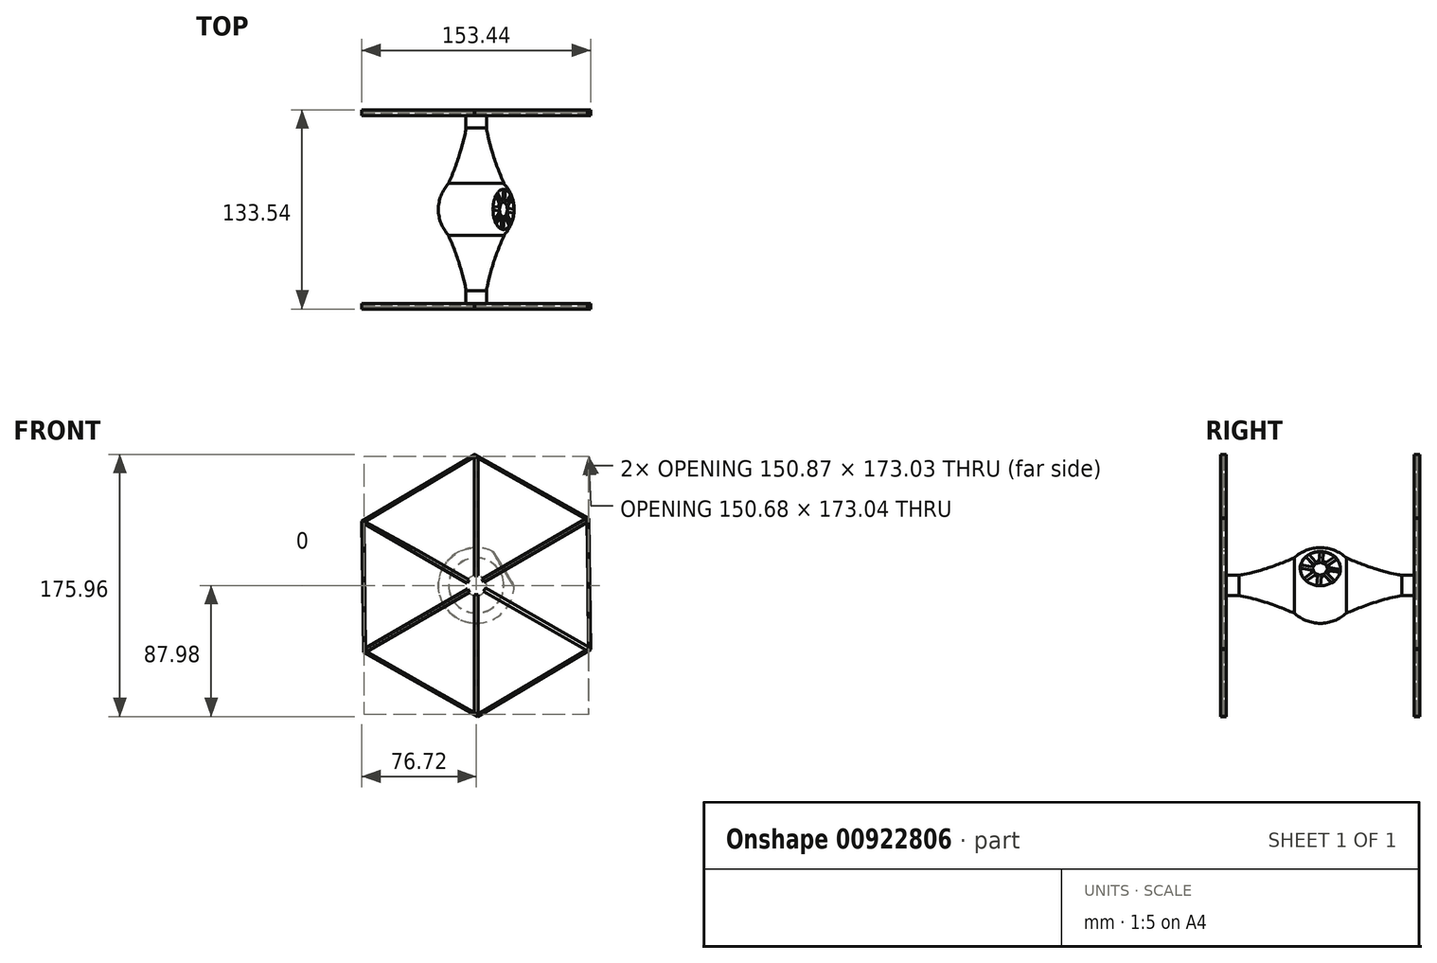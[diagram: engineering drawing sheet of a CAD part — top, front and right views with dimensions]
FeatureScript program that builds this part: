
annotation { "Feature Type Name" : "Feature", "Feature Type Description" : "" }
export const myFeature = defineFeature(function(context is Context, id is Id, definition is map)
    precondition{}
    {
        {
            var Q0;
            Q0=qCreatedBy(makeId("Front.planeOp"),FACE);
            var sketch = newSketch(context, id + "F0", { "sketchPlane" : qUnion([Q0])});
            skArc(sketch, "E0", {"start": v(0, 25.4) * mm, "mid": v(25.4, 0) * mm, "end": v(0, -25.4) * mm});
            skLineSegment(sketch, "E1", {"start": v(0, 25.4) * mm, "end": v(0, -25.4) * mm});
            skSolve(sketch);
        }
        {
            var Q0;
            Q0=qSketchRegion(id+"F0",true);
            var Q1;
            Q1=sQuery(id+"F0.wireOp",EDGE,"E1");
            revolve(context, id + "F1", {"surfaceOperationType" : NewSurfaceOperationType.NEW, "entities" : qUnion([Q0]), "axis" : qUnion([Q1]), "revolveType" : RevolveType.ONE_DIRECTION, "angle" : 180 * degree});
        }
        {
            var Q0;
            Q0=qCreatedBy(makeId("Right.planeOp"),FACE);
            var sketch = newSketch(context, id + "F2", { "sketchPlane" : qUnion([Q0])});
            skLineSegment(sketch, "E2", {"start": v(-62.96, 0) * mm, "end": v(0, 0) * mm});
            skLineSegment(sketch, "E3", {"start": v(-62.96, 0) * mm, "end": v(-62.96, 6.88) * mm});
            skFitSpline(sketch, "E4", {"points": [v(-62.96, 6.88) * mm, v(-54.61, 6.88) * mm, v(-33.5, 12.3) * mm, v(-17.49, 18.56) * mm], "startDerivative": vector(40.65, 0) * mm, "endDerivative": vector(41.74, 17.6) * mm});
            skLineSegment(sketch, "E5", {"start": v(-17.49, 18.56) * mm, "end": v(-17.49, 0) * mm});
            skLineSegment(sketch, "E6", {"start": v(-62.96, 6.88) * mm, "end": v(-50.15, 6.88) * mm});
            skSolve(sketch);
        }
        {
            var Q0;
            Q0=qSketchRegion(id+"F2",true);
            var Q1;
            Q1=sQuery(id+"F2.wireOp",EDGE,"E2");
            revolve(context, id + "F3", {"operationType" : NewBodyOperationType.ADD, "surfaceOperationType" : NewSurfaceOperationType.NEW, "entities" : qUnion([Q0]), "axis" : qUnion([Q1]), "revolveType" : RevolveType.FULL});
        }
        {
            var Q0;
            Q0=qCreatedBy(makeId("Front.planeOp"),FACE);
            var sketch = newSketch(context, id + "F4", { "sketchPlane" : qUnion([Q0])});
            skLineSegment(sketch, "E7", {"start": v(18.07, 11.14) * mm, "end": v(0, 0) * mm});
            skSolve(sketch);
        }
        {
            var Q0;
            Q0=makeQuery(id+"F3.opRevolve","SWEPT_FACE",FACE,{"disambiguationData":[OSD([sQuery(id+"F2.wireOp",EDGE,"E3")])]});
            cPlane(context, id + "F5", {"entities" : qUnion([Q0]), "cplaneType" : CPlaneType.OFFSET, "offset" : 0 * mm, "width" : 152.4 * mm, "height" : 152.4 * mm});
        }
        {
            var Q0;
            Q0=qCreatedBy(id+"F5.planeOp",FACE);
            var sketch = newSketch(context, id + "F6", { "sketchPlane" : qUnion([Q0])});
            skCircle(sketch, "E8.cCircle", {"center": v(0, 0) * mm, "radius": 76.2 * mm, "construction": true});
            skLineSegment(sketch, "E8.0", {"start": v(76.62, -43.26) * mm, "end": v(0.84, -87.98) * mm});
            skLineSegment(sketch, "E8.1", {"start": v(0.84, -87.98) * mm, "end": v(-75.78, -44.72) * mm});
            skLineSegment(sketch, "E8.2", {"start": v(-75.78, -44.72) * mm, "end": v(-76.62, 43.26) * mm});
            skLineSegment(sketch, "E8.3", {"start": v(-76.62, 43.26) * mm, "end": v(-0.84, 87.98) * mm});
            skLineSegment(sketch, "E8.4", {"start": v(-0.84, 87.98) * mm, "end": v(75.78, 44.72) * mm});
            skLineSegment(sketch, "E8.5", {"start": v(75.78, 44.72) * mm, "end": v(76.62, -43.26) * mm});
            skPoint(sketch, "E8.0.midPoint", {"position": v(38.73, -65.62) * mm});
            skSolve(sketch);
        }
        {
            var Q0;
            Q0=qSketchRegion(id+"F6",true);
            extrude(context, id + "F7", {"entities" : qUnion([Q0]), "depth" : 2.54 * mm, "offsetDistance" : 25.4 * mm});
        }
        {
            var Q0;
            Q0=makeQuery(id+"F7.opExtrude","CAP_FACE",FACE,{"disambiguationData":[OSD([sQuery(id+"F6.wireOp",EDGE,"E8.0"),sQuery(id+"F6.wireOp",EDGE,"E8.1"),sQuery(id+"F6.wireOp",EDGE,"E8.2"),sQuery(id+"F6.wireOp",EDGE,"E8.3"),sQuery(id+"F6.wireOp",EDGE,"E8.4"),sQuery(id+"F6.wireOp",EDGE,"E8.5")])],"isStart":false});
            shell(context, id + "F8", {"entities" : qUnion([Q0]), "thickness" : 1.27 * mm});
        }
        {
            var Q0;
            Q0=qCreatedBy(id+"F5.planeOp",FACE);
            var sketch = newSketch(context, id + "F9", { "sketchPlane" : qUnion([Q0])});
            skLineSegment(sketch, "E9", {"start": v(0, 92.99) * mm, "end": v(0, 6.47) * mm, "construction": true});
            skLineSegment(sketch, "E10", {"start": v(-80.5, 45.9) * mm, "end": v(-5.53, 2.72) * mm, "construction": true});
            skLineSegment(sketch, "E11", {"start": v(5.53, -2.69) * mm, "end": v(80.5, -45.88) * mm, "construction": true});
            skLineSegment(sketch, "E12", {"start": v(0, -6.03) * mm, "end": v(0, -92.55) * mm});
            skLineSegment(sketch, "E13", {"start": v(-80, -46.75) * mm, "end": v(-5.12, -3.4) * mm, "construction": true});
            skLineSegment(sketch, "E14", {"start": v(4.34, 3.22) * mm, "end": v(79.21, 46.57) * mm, "construction": true});
            skLineSegment(sketch, "E15", {"start": v(-1.27, -6.03) * mm, "end": v(1.27, -6.03) * mm});
            skLineSegment(sketch, "E16", {"start": v(4.9, -3.79) * mm, "end": v(6.17, -1.59) * mm});
            skLineSegment(sketch, "E17", {"start": v(3.7, 4.32) * mm, "end": v(4.97, 2.12) * mm});
            skLineSegment(sketch, "E18", {"start": v(3.7, 4.32) * mm, "end": v(78.58, 47.67) * mm});
            skLineSegment(sketch, "E19", {"start": v(4.97, 2.12) * mm, "end": v(79.85, 45.47) * mm});
            skLineSegment(sketch, "E20", {"start": v(-1.27, 6.47) * mm, "end": v(1.27, 6.47) * mm});
            skLineSegment(sketch, "E21", {"start": v(-6.17, 1.62) * mm, "end": v(-4.9, 3.82) * mm});
            skLineSegment(sketch, "E22", {"start": v(-4.4, -4.44) * mm, "end": v(-5.84, -2.36) * mm});
            skLineSegment(sketch, "E23", {"start": v(-4.9, 3.82) * mm, "end": v(-38.95, 23.43) * mm});
            skLineSegment(sketch, "E24", {"start": v(-6.17, 1.62) * mm, "end": v(-81.14, 44.8) * mm});
            skLineSegment(sketch, "E25", {"start": v(-4.4, -4.44) * mm, "end": v(-79.27, -47.8) * mm});
            skLineSegment(sketch, "E26", {"start": v(-5.84, -2.36) * mm, "end": v(-80, -45.29) * mm});
            skLineSegment(sketch, "E27", {"start": v(4.9, -3.79) * mm, "end": v(79.87, -46.98) * mm});
            skLineSegment(sketch, "E28", {"start": v(6.17, -1.59) * mm, "end": v(81.14, -44.78) * mm});
            skLineSegment(sketch, "E29", {"start": v(-1.27, 6.47) * mm, "end": v(-1.27, 92.99) * mm});
            skLineSegment(sketch, "E30", {"start": v(1.27, 6.47) * mm, "end": v(1.27, 92.99) * mm});
            skLineSegment(sketch, "E31", {"start": v(1.27, -6.03) * mm, "end": v(1.27, -92.55) * mm});
            skLineSegment(sketch, "E32", {"start": v(-1.27, -6.03) * mm, "end": v(-1.27, -92.55) * mm});
            skLineSegment(sketch, "E33", {"start": v(1.27, -92.55) * mm, "end": v(0, -92.55) * mm});
            skLineSegment(sketch, "E34", {"start": v(0, -92.55) * mm, "end": v(-1.27, -92.55) * mm});
            skLineSegment(sketch, "E35", {"start": v(81.14, -44.78) * mm, "end": v(80.5, -45.88) * mm});
            skLineSegment(sketch, "E36", {"start": v(79.87, -46.98) * mm, "end": v(80.5, -45.88) * mm});
            skLineSegment(sketch, "E37", {"start": v(79.21, 46.57) * mm, "end": v(79.85, 45.47) * mm});
            skLineSegment(sketch, "E38", {"start": v(79.21, 46.57) * mm, "end": v(78.58, 47.67) * mm});
            skLineSegment(sketch, "E39", {"start": v(1.27, 92.99) * mm, "end": v(0, 92.99) * mm});
            skLineSegment(sketch, "E40", {"start": v(-1.27, 92.99) * mm, "end": v(0, 92.99) * mm});
            skLineSegment(sketch, "E41", {"start": v(0, 92.99) * mm, "end": v(-1.27, 92.99) * mm});
            skLineSegment(sketch, "E42", {"start": v(-81.14, 44.8) * mm, "end": v(-80.5, 45.9) * mm});
            skLineSegment(sketch, "E43", {"start": v(-38.95, 23.43) * mm, "end": v(-80.5, 45.9) * mm});
            skLineSegment(sketch, "E44", {"start": v(-80, -45.29) * mm, "end": v(-80, -46.75) * mm});
            skLineSegment(sketch, "E45", {"start": v(-79.27, -47.8) * mm, "end": v(-80, -46.75) * mm});
            skSolve(sketch);
        }
        {
            var Q0;
            Q0=qSketchRegion(id+"F9",true);
            extrude(context, id + "F10", {"entities" : qUnion([Q0]), "depth" : 2.54 * mm, "offsetDistance" : 25.4 * mm});
        }
        {
            var Q0;
            Q0=qCreatedBy(id+"F5.planeOp",FACE);
            var sketch = newSketch(context, id + "F11", { "sketchPlane" : qUnion([Q0])});
            skCircle(sketch, "E46.cCircle", {"center": v(0, 0) * mm, "radius": 76.2 * mm, "construction": true});
            skLineSegment(sketch, "E46.0", {"start": v(1.03, -87.98) * mm, "end": v(-75.68, -44.89) * mm});
            skLineSegment(sketch, "E46.1", {"start": v(-75.68, -44.89) * mm, "end": v(-76.71, 43.1) * mm});
            skLineSegment(sketch, "E46.2", {"start": v(-76.71, 43.1) * mm, "end": v(-1.03, 87.98) * mm});
            skLineSegment(sketch, "E46.3", {"start": v(-1.03, 87.98) * mm, "end": v(75.68, 44.89) * mm});
            skLineSegment(sketch, "E46.4", {"start": v(75.68, 44.89) * mm, "end": v(76.71, -43.1) * mm});
            skLineSegment(sketch, "E46.5", {"start": v(76.71, -43.1) * mm, "end": v(1.03, -87.98) * mm});
            skPoint(sketch, "E46.0.midPoint", {"position": v(-37.32, -66.43) * mm});
            skCircle(sketch, "E47.cCircle", {"center": v(0, 0) * mm, "radius": 74.93 * mm, "construction": true});
            skLineSegment(sketch, "E47.0", {"start": v(75.43, -42.38) * mm, "end": v(1.02, -86.52) * mm});
            skLineSegment(sketch, "E47.1", {"start": v(1.02, -86.52) * mm, "end": v(-74.42, -44.14) * mm});
            skLineSegment(sketch, "E47.2", {"start": v(-74.42, -44.14) * mm, "end": v(-75.43, 42.38) * mm});
            skLineSegment(sketch, "E47.3", {"start": v(-75.43, 42.38) * mm, "end": v(-1.02, 86.52) * mm});
            skLineSegment(sketch, "E47.4", {"start": v(-1.02, 86.52) * mm, "end": v(74.42, 44.14) * mm});
            skLineSegment(sketch, "E47.5", {"start": v(74.42, 44.14) * mm, "end": v(75.43, -42.38) * mm});
            skPoint(sketch, "E47.0.midPoint", {"position": v(38.23, -64.45) * mm});
            skLineSegment(sketch, "E48", {"start": v(0, 0) * mm, "end": v(-1.02, 86.52) * mm, "construction": true});
            skSolve(sketch);
        }
        {
            var Q0;
            Q0=qSketchRegion(id+"F11",true);
            extrude(context, id + "F12", {"entities" : qUnion([Q0]), "depth" : 3.8 * mm, "offsetDistance" : 25.4 * mm});
        }
        {
            var Q0;
            Q0=qCreatedBy(id+"F5.planeOp",FACE);
            var sketch = newSketch(context, id + "F13", { "sketchPlane" : qUnion([Q0])});
            skCircle(sketch, "E49.cCircle", {"center": v(0, 0) * mm, "radius": 76.2 * mm, "construction": true});
            skLineSegment(sketch, "E49.0", {"start": v(1.05, -87.98) * mm, "end": v(-75.67, -44.9) * mm});
            skLineSegment(sketch, "E49.1", {"start": v(-75.67, -44.9) * mm, "end": v(-76.72, 43.08) * mm});
            skLineSegment(sketch, "E49.2", {"start": v(-76.72, 43.08) * mm, "end": v(-1.05, 87.98) * mm});
            skLineSegment(sketch, "E49.3", {"start": v(-1.05, 87.98) * mm, "end": v(75.67, 44.9) * mm});
            skLineSegment(sketch, "E49.4", {"start": v(75.67, 44.9) * mm, "end": v(76.72, -43.08) * mm});
            skLineSegment(sketch, "E49.5", {"start": v(76.72, -43.08) * mm, "end": v(1.05, -87.98) * mm});
            skPoint(sketch, "E49.0.midPoint", {"position": v(-37.31, -66.44) * mm});
            skCircle(sketch, "E50.cCircle", {"center": v(0, 0) * mm, "radius": 151.68 * mm, "construction": true});
            skLineSegment(sketch, "E50.0", {"start": v(-149.87, -90.64) * mm, "end": v(-153.43, 84.47) * mm});
            skLineSegment(sketch, "E50.1", {"start": v(-153.43, 84.47) * mm, "end": v(-3.56, 175.11) * mm});
            skLineSegment(sketch, "E50.2", {"start": v(-3.56, 175.11) * mm, "end": v(149.87, 90.64) * mm});
            skLineSegment(sketch, "E50.3", {"start": v(149.87, 90.64) * mm, "end": v(153.43, -84.47) * mm});
            skLineSegment(sketch, "E50.4", {"start": v(153.43, -84.47) * mm, "end": v(3.56, -175.11) * mm});
            skLineSegment(sketch, "E50.5", {"start": v(3.56, -175.11) * mm, "end": v(-149.87, -90.64) * mm});
            skPoint(sketch, "E50.0.midPoint", {"position": v(-151.65, -3.09) * mm});
            skSolve(sketch);
        }
        {
            var Q0;
            Q0=qSketchRegion(id+"F13",true);
            extrude(context, id + "F14", {"entities" : qUnion([Q0]), "operationType" : NewBodyOperationType.REMOVE, "depth" : 101.6 * mm, "offsetDistance" : 25.4 * mm});
        }
        {
            var Q0;
            Q0=makeQuery(id+"F1.opRevolve","SWEPT_BODY",BODY,{"disambiguationData":[OSD([sQuery(id+"F0.wireOp",EDGE,"E0"),sQuery(id+"F0.wireOp",EDGE,"E1")])]});
            var Q1;
            Q1=makeQuery(id+"F12.opExtrude","SWEPT_BODY",BODY,{"disambiguationData":[OSD([sQuery(id+"F11.wireOp",EDGE,"E46.0"),sQuery(id+"F11.wireOp",EDGE,"E46.1"),sQuery(id+"F11.wireOp",EDGE,"E46.2"),sQuery(id+"F11.wireOp",EDGE,"E46.3"),sQuery(id+"F11.wireOp",EDGE,"E46.4"),sQuery(id+"F11.wireOp",EDGE,"E46.5"),sQuery(id+"F11.wireOp",EDGE,"E47.0"),sQuery(id+"F11.wireOp",EDGE,"E47.1"),sQuery(id+"F11.wireOp",EDGE,"E47.2"),sQuery(id+"F11.wireOp",EDGE,"E47.3"),sQuery(id+"F11.wireOp",EDGE,"E47.4"),sQuery(id+"F11.wireOp",EDGE,"E47.5")])]});
            var Q2;
            Q2=makeQuery(id+"F10.opExtrude","SWEPT_BODY",BODY,{"disambiguationData":[OSD([sQuery(id+"F9.wireOp",EDGE,"E17"),sQuery(id+"F9.wireOp",EDGE,"E18"),sQuery(id+"F9.wireOp",EDGE,"E19"),sQuery(id+"F9.wireOp",EDGE,"E37"),sQuery(id+"F9.wireOp",EDGE,"E38")])]});
            var Q3;
            Q3=makeQuery(id+"F7.opExtrude","SWEPT_BODY",BODY,{"disambiguationData":[OSD([sQuery(id+"F6.wireOp",EDGE,"E8.0"),sQuery(id+"F6.wireOp",EDGE,"E8.1"),sQuery(id+"F6.wireOp",EDGE,"E8.2"),sQuery(id+"F6.wireOp",EDGE,"E8.3"),sQuery(id+"F6.wireOp",EDGE,"E8.4"),sQuery(id+"F6.wireOp",EDGE,"E8.5")])]});
            var Q4;
            Q4=makeQuery(id+"F10.opExtrude","SWEPT_BODY",BODY,{"disambiguationData":[OSD([sQuery(id+"F9.wireOp",EDGE,"E16"),sQuery(id+"F9.wireOp",EDGE,"E27"),sQuery(id+"F9.wireOp",EDGE,"E28"),sQuery(id+"F9.wireOp",EDGE,"E35"),sQuery(id+"F9.wireOp",EDGE,"E36")])]});
            var Q5;
            Q5=makeQuery(id+"F10.opExtrude","SWEPT_BODY",BODY,{"disambiguationData":[OSD([sQuery(id+"F9.wireOp",EDGE,"E15"),sQuery(id+"F9.wireOp",EDGE,"E31"),sQuery(id+"F9.wireOp",EDGE,"E32"),sQuery(id+"F9.wireOp",EDGE,"E33"),sQuery(id+"F9.wireOp",EDGE,"E34")])]});
            var Q6;
            Q6=makeQuery(id+"F10.opExtrude","SWEPT_BODY",BODY,{"disambiguationData":[OSD([sQuery(id+"F9.wireOp",EDGE,"E21"),sQuery(id+"F9.wireOp",EDGE,"E23"),sQuery(id+"F9.wireOp",EDGE,"E24"),sQuery(id+"F9.wireOp",EDGE,"E42"),sQuery(id+"F9.wireOp",EDGE,"E43")])]});
            var Q7;
            Q7=makeQuery(id+"F10.opExtrude","SWEPT_BODY",BODY,{"disambiguationData":[OSD([sQuery(id+"F9.wireOp",EDGE,"E20"),sQuery(id+"F9.wireOp",EDGE,"E29"),sQuery(id+"F9.wireOp",EDGE,"E30"),sQuery(id+"F9.wireOp",EDGE,"E39"),sQuery(id+"F9.wireOp",EDGE,"E41")])]});
            var Q8;
            Q8=makeQuery(id+"F10.opExtrude","SWEPT_BODY",BODY,{"disambiguationData":[OSD([sQuery(id+"F9.wireOp",EDGE,"E22"),sQuery(id+"F9.wireOp",EDGE,"E25"),sQuery(id+"F9.wireOp",EDGE,"E26"),sQuery(id+"F9.wireOp",EDGE,"E44"),sQuery(id+"F9.wireOp",EDGE,"E45")])]});
            var Q9;
            Q9=qCreatedBy(makeId("Front.planeOp"),FACE);
            mirror(context, id + "F15", {"entities" : qUnion([Q0, Q1, Q2, Q3, Q4, Q5, Q6, Q7, Q8]), "mirrorPlane" : qUnion([Q9])});
        }
        {
            var Q0;
            Q0=sQuery(id+"F4.wireOp",VERTEX,"E7.start");
            var Q1;
            Q1=sQuery(id+"F4.wireOp",EDGE,"E7");
            cPlane(context, id + "F16", {"entities" : qUnion([Q0, Q1]), "cplaneType" : CPlaneType.CURVE_POINT, "offset" : 25.4 * mm, "width" : 152.4 * mm, "height" : 152.4 * mm});
        }
        {
            var Q0;
            Q0=qCreatedBy(id+"F16.planeOp",FACE);
            var sketch = newSketch(context, id + "F17", { "sketchPlane" : qUnion([Q0])});
            skCircle(sketch, "E51", {"center": v(0, 0) * mm, "radius": 13.5 * mm});
            skSolve(sketch);
        }
        {
            var Q0;
            Q0=qSketchRegion(id+"F17",true);
            extrude(context, id + "F18", {"entities" : qUnion([Q0]), "operationType" : NewBodyOperationType.REMOVE, "oppositeDirection" : true, "depth" : 25.4 * mm, "offsetDistance" : 25.4 * mm});
        }
        {
            var Q0;
            Q0=qCreatedBy(id+"F16.planeOp",FACE);
            var sketch = newSketch(context, id + "F19", { "sketchPlane" : qUnion([Q0])});
            skCircle(sketch, "E52.cCircle", {"center": v(0, 0) * mm, "radius": 6.1 * mm, "construction": true});
            skLineSegment(sketch, "E52.0", {"start": v(0.45, -6.6) * mm, "end": v(-4.34, -4.98) * mm});
            skLineSegment(sketch, "E52.1", {"start": v(-4.34, -4.98) * mm, "end": v(-6.6, -0.45) * mm});
            skLineSegment(sketch, "E52.2", {"start": v(-6.6, -0.45) * mm, "end": v(-4.98, 4.34) * mm});
            skLineSegment(sketch, "E52.3", {"start": v(-4.98, 4.34) * mm, "end": v(-0.45, 6.6) * mm});
            skLineSegment(sketch, "E52.4", {"start": v(-0.45, 6.6) * mm, "end": v(4.34, 4.98) * mm});
            skLineSegment(sketch, "E52.5", {"start": v(4.34, 4.98) * mm, "end": v(6.6, 0.45) * mm});
            skLineSegment(sketch, "E52.6", {"start": v(6.6, 0.45) * mm, "end": v(4.98, -4.34) * mm});
            skLineSegment(sketch, "E52.7", {"start": v(4.98, -4.34) * mm, "end": v(0.45, -6.6) * mm});
            skPoint(sketch, "E52.0.midPoint", {"position": v(-1.95, -5.78) * mm});
            skLineSegment(sketch, "E53", {"start": v(-0.45, 6.6) * mm, "end": v(-0.87, 13.38) * mm, "construction": true});
            skLineSegment(sketch, "E54", {"start": v(4.34, 4.98) * mm, "end": v(8.62, 10.27) * mm, "construction": true});
            skLineSegment(sketch, "E55", {"start": v(-4.98, 4.34) * mm, "end": v(-10.46, 8.47) * mm, "construction": true});
            skLineSegment(sketch, "E56", {"start": v(-6.6, -0.45) * mm, "end": v(-13.35, -1.73) * mm, "construction": true});
            skLineSegment(sketch, "E57", {"start": v(-4.34, -4.98) * mm, "end": v(-8.67, -10.4) * mm, "construction": true});
            skLineSegment(sketch, "E58", {"start": v(0.45, -6.6) * mm, "end": v(1.08, -13.42) * mm, "construction": true});
            skLineSegment(sketch, "E59", {"start": v(4.98, -4.34) * mm, "end": v(10.28, -8.68) * mm, "construction": true});
            skLineSegment(sketch, "E60", {"start": v(6.6, 0.45) * mm, "end": v(13.35, 1.77) * mm, "construction": true});
            skLineSegment(sketch, "E61", {"start": v(7.59, 11.13) * mm, "end": v(9.66, 9.42) * mm});
            skLineSegment(sketch, "E62", {"start": v(7.59, 11.13) * mm, "end": v(2.92, 5.46) * mm});
            skLineSegment(sketch, "E63", {"start": v(9.66, 9.42) * mm, "end": v(5, 3.66) * mm});
            skLineSegment(sketch, "E64", {"start": v(-2.1, 13.3) * mm, "end": v(0.37, 13.45) * mm});
            skLineSegment(sketch, "E65", {"start": v(-2.1, 13.3) * mm, "end": v(-1.65, 6) * mm});
            skLineSegment(sketch, "E66", {"start": v(0.37, 13.45) * mm, "end": v(0.8, 6.17) * mm});
            skCircle(sketch, "E67.cCircle", {"center": v(0, 0) * mm, "radius": 4.83 * mm, "construction": true});
            skLineSegment(sketch, "E67.0", {"start": v(4, -3.37) * mm, "end": v(0.45, -5.21) * mm});
            skLineSegment(sketch, "E67.1", {"start": v(0.45, -5.21) * mm, "end": v(-3.37, -4) * mm});
            skLineSegment(sketch, "E67.2", {"start": v(-3.37, -4) * mm, "end": v(-5.21, -0.45) * mm});
            skLineSegment(sketch, "E67.3", {"start": v(-5.21, -0.45) * mm, "end": v(-4, 3.37) * mm});
            skLineSegment(sketch, "E67.4", {"start": v(-4, 3.37) * mm, "end": v(-0.45, 5.21) * mm});
            skLineSegment(sketch, "E67.5", {"start": v(-0.45, 5.21) * mm, "end": v(3.37, 4) * mm});
            skLineSegment(sketch, "E67.6", {"start": v(3.37, 4) * mm, "end": v(5.21, 0.45) * mm});
            skLineSegment(sketch, "E67.7", {"start": v(5.21, 0.45) * mm, "end": v(4, -3.37) * mm});
            skPoint(sketch, "E67.0.midPoint", {"position": v(2.23, -4.3) * mm});
            skLineSegment(sketch, "E68", {"start": v(-11.23, 7.47) * mm, "end": v(-9.7, 9.47) * mm});
            skLineSegment(sketch, "E69", {"start": v(-9.7, 9.47) * mm, "end": v(-3.79, 4.93) * mm});
            skLineSegment(sketch, "E70", {"start": v(-11.23, 7.47) * mm, "end": v(-5.43, 3) * mm});
            skLineSegment(sketch, "E71", {"start": v(-13.57, -0.58) * mm, "end": v(-13.13, -2.87) * mm});
            skLineSegment(sketch, "E72", {"start": v(-13.13, -2.87) * mm, "end": v(-6.05, -1.53) * mm});
            skLineSegment(sketch, "E73", {"start": v(-13.57, -0.58) * mm, "end": v(-6.16, 0.82) * mm});
            skLineSegment(sketch, "E74", {"start": v(-9.64, -9.57) * mm, "end": v(-7.71, -11.23) * mm});
            skLineSegment(sketch, "E75", {"start": v(-9.64, -9.57) * mm, "end": v(-4.83, -4) * mm});
            skLineSegment(sketch, "E76", {"start": v(-7.71, -11.23) * mm, "end": v(-3.06, -5.4) * mm});
            skLineSegment(sketch, "E77", {"start": v(2.34, -13.3) * mm, "end": v(-0.19, -13.53) * mm});
            skLineSegment(sketch, "E78", {"start": v(-0.19, -13.53) * mm, "end": v(-0.87, -6.15) * mm});
            skLineSegment(sketch, "E79", {"start": v(2.34, -13.3) * mm, "end": v(1.67, -5.99) * mm});
            skLineSegment(sketch, "E80", {"start": v(9.46, -9.68) * mm, "end": v(11.1, -7.67) * mm});
            skLineSegment(sketch, "E81", {"start": v(9.46, -9.68) * mm, "end": v(3.7, -4.98) * mm});
            skLineSegment(sketch, "E82", {"start": v(11.1, -7.67) * mm, "end": v(5.42, -3.03) * mm});
            skLineSegment(sketch, "E83", {"start": v(13.1, 3.01) * mm, "end": v(13.6, 0.52) * mm});
            skLineSegment(sketch, "E84", {"start": v(13.1, 3.01) * mm, "end": v(6, 1.63) * mm});
            skLineSegment(sketch, "E85", {"start": v(13.6, 0.52) * mm, "end": v(6.13, -0.93) * mm});
            skSolve(sketch);
        }
        {
            var Q0;
            Q0=qSketchRegion(id+"F19",true);
            extrude(context, id + "F20", {"entities" : qUnion([Q0]), "operationType" : NewBodyOperationType.ADD, "oppositeDirection" : true, "depth" : 0.25 * mm, "offsetDistance" : 25.4 * mm});
        }
    });
